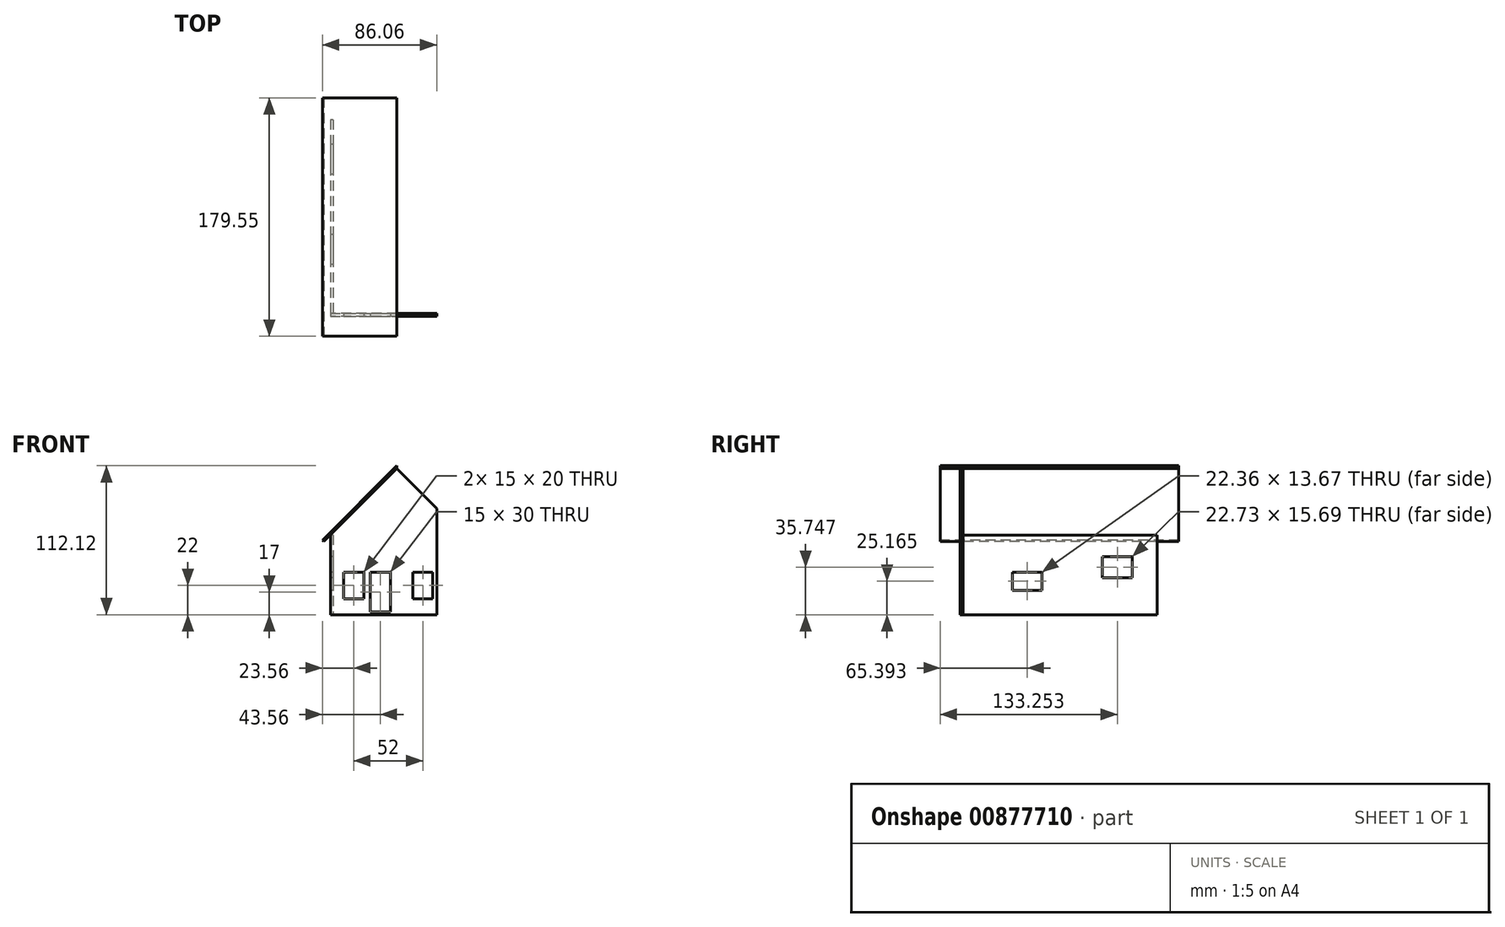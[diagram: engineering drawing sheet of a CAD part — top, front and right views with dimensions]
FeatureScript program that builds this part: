
annotation { "Feature Type Name" : "Feature", "Feature Type Description" : "" }
export const myFeature = defineFeature(function(context is Context, id is Id, definition is map)
    precondition{}
    {
        {
            var Q0;
            Q0=qCreatedBy(makeId("Top.planeOp"),FACE);
            var sketch = newSketch(context, id + "F0", { "sketchPlane" : qUnion([Q0])});
            skLineSegment(sketch, "E0.bottom", {"start": v(-80, 150) * mm, "end": v(0, 150) * mm});
            skLineSegment(sketch, "E0.top", {"start": v(-80, 0) * mm, "end": v(0, 0) * mm});
            skLineSegment(sketch, "E0.left", {"start": v(-80, 150) * mm, "end": v(-80, 0) * mm});
            skLineSegment(sketch, "E0.right", {"start": v(0, 150) * mm, "end": v(0, 0) * mm});
            skLineSegment(sketch, "E1", {"start": v(-80, 2) * mm, "end": v(0, 2) * mm});
            skLineSegment(sketch, "E2", {"start": v(-80, 148) * mm, "end": v(0, 148) * mm});
            skLineSegment(sketch, "E3", {"start": v(-78, 148) * mm, "end": v(-78, 2) * mm});
            skLineSegment(sketch, "E4", {"start": v(-2, 148) * mm, "end": v(-2, 2) * mm});
            skSolve(sketch);
        }
        {
            var Q0;
            Q0=qCreatedBy(makeId("Front.planeOp"),FACE);
            var sketch = newSketch(context, id + "F1", { "sketchPlane" : qUnion([Q0])});
            skLineSegment(sketch, "E5", {"start": v(-80, 0) * mm, "end": v(0, 0) * mm});
            skLineSegment(sketch, "E6", {"start": v(0, 0) * mm, "end": v(0, 80) * mm});
            skLineSegment(sketch, "E7", {"start": v(0, 80) * mm, "end": v(-30, 110) * mm});
            skLineSegment(sketch, "E8", {"start": v(-30, 110) * mm, "end": v(-80, 60) * mm});
            skLineSegment(sketch, "E9", {"start": v(-80, 60) * mm, "end": v(-80, 0) * mm});
            skLineSegment(sketch, "E10.bottom", {"start": v(-70, 32) * mm, "end": v(-55, 32) * mm});
            skLineSegment(sketch, "E10.top", {"start": v(-70, 12) * mm, "end": v(-55, 12) * mm});
            skLineSegment(sketch, "E10.left", {"start": v(-70, 32) * mm, "end": v(-70, 12) * mm});
            skLineSegment(sketch, "E10.right", {"start": v(-55, 32) * mm, "end": v(-55, 12) * mm});
            skLineSegment(sketch, "E11.bottom", {"start": v(-18, 32) * mm, "end": v(-3, 32) * mm});
            skLineSegment(sketch, "E11.top", {"start": v(-18, 12) * mm, "end": v(-3, 12) * mm});
            skLineSegment(sketch, "E11.left", {"start": v(-18, 32) * mm, "end": v(-18, 12) * mm});
            skLineSegment(sketch, "E11.right", {"start": v(-3, 32) * mm, "end": v(-3, 12) * mm});
            skLineSegment(sketch, "E12.bottom", {"start": v(-50, 32) * mm, "end": v(-35, 32) * mm});
            skLineSegment(sketch, "E12.top", {"start": v(-50, 2) * mm, "end": v(-35, 2) * mm});
            skLineSegment(sketch, "E12.left", {"start": v(-50, 32) * mm, "end": v(-50, 2) * mm});
            skLineSegment(sketch, "E12.right", {"start": v(-35, 32) * mm, "end": v(-35, 2) * mm});
            skSolve(sketch);
        }
        {
            var Q0;
            Q0=makeQuery(id+"F1.imprint","IMPRINT",FACE,{"disambiguationData":[TD([[makeQuery(id+"F1.imprint","IMPRINT",EDGE,{"derivedFrom":sQuery(id+"F1.wireOp",EDGE,"E5")}),1.0]])]});
            var Q1;
            Q1=sQuery(id+"F0.wireOp",VERTEX,"E1.end");
            extrude(context, id + "F2", {"entities" : qUnion([Q0]), "endBound" : BoundingType.UP_TO_VERTEX, "oppositeDirection" : true, "depth" : 25 * mm, "endBoundEntityVertex" : qUnion([Q1]), "offsetDistance" : 25 * mm});
        }
        {
            var Q0;
            Q0=qCreatedBy(makeId("Right.planeOp"),FACE);
            var Q1;
            Q1=sQuery(id+"F0.wireOp",VERTEX,"E0.top.start");
            cPlane(context, id + "F3", {"entities" : qUnion([Q0, Q1]), "cplaneType" : CPlaneType.PLANE_POINT, "offset" : 25 * mm, "width" : 150 * mm, "height" : 150 * mm});
        }
        {
            var Q0;
            Q0=qCreatedBy(id+"F3.planeOp",FACE);
            var sketch = newSketch(context, id + "F4", { "sketchPlane" : qUnion([Q0])});
            skLineSegment(sketch, "E13.bottom", {"start": v(148, 60) * mm, "end": v(2, 60) * mm});
            skLineSegment(sketch, "E13.top", {"start": v(148, 0) * mm, "end": v(2, 0) * mm});
            skLineSegment(sketch, "E13.left", {"start": v(148, 60) * mm, "end": v(148, 0) * mm});
            skLineSegment(sketch, "E13.right", {"start": v(2, 60) * mm, "end": v(2, 0) * mm});
            skLineSegment(sketch, "E14.bottom", {"start": v(129.5, 43.6) * mm, "end": v(106.78, 43.6) * mm});
            skLineSegment(sketch, "E14.top", {"start": v(129.5, 27.9) * mm, "end": v(106.78, 27.9) * mm});
            skLineSegment(sketch, "E14.left", {"start": v(129.5, 43.6) * mm, "end": v(129.5, 27.9) * mm});
            skLineSegment(sketch, "E14.right", {"start": v(106.78, 43.6) * mm, "end": v(106.78, 27.9) * mm});
            skLineSegment(sketch, "E15.bottom", {"start": v(61.46, 32) * mm, "end": v(39.1, 32) * mm});
            skLineSegment(sketch, "E15.top", {"start": v(61.46, 18.33) * mm, "end": v(39.1, 18.33) * mm});
            skLineSegment(sketch, "E15.left", {"start": v(61.46, 32) * mm, "end": v(61.46, 18.33) * mm});
            skLineSegment(sketch, "E15.right", {"start": v(39.1, 32) * mm, "end": v(39.1, 18.33) * mm});
            skLineSegment(sketch, "E16.bottom", {"start": v(164.44, 109.45) * mm, "end": v(-15.11, 109.45) * mm});
            skLineSegment(sketch, "E16.top", {"start": v(164.44, 62.44) * mm, "end": v(-15.11, 62.44) * mm});
            skLineSegment(sketch, "E16.left", {"start": v(164.44, 109.45) * mm, "end": v(164.44, 62.44) * mm});
            skLineSegment(sketch, "E16.right", {"start": v(-15.11, 109.45) * mm, "end": v(-15.11, 62.44) * mm});
            skSolve(sketch);
        }
        {
            var Q0;
            Q0=makeQuery(id+"F4.imprint","IMPRINT",FACE,{"disambiguationData":[TD([[makeQuery(id+"F4.imprint","IMPRINT",EDGE,{"derivedFrom":sQuery(id+"F4.wireOp",EDGE,"E13.bottom")}),1.0]])]});
            var Q1;
            Q1=sQuery(id+"F0.wireOp",VERTEX,"E3.end");
            extrude(context, id + "F5", {"entities" : qUnion([Q0]), "endBound" : BoundingType.UP_TO_VERTEX, "depth" : 25 * mm, "endBoundEntityVertex" : qUnion([Q1]), "offsetDistance" : 25 * mm});
        }
        {
            var Q0;
            Q0=qCreatedBy(makeId("Front.planeOp"),FACE);
            var sketch = newSketch(context, id + "F6", { "sketchPlane" : qUnion([Q0])});
            skLineSegment(sketch, "E17", {"start": v(-30, 112.12) * mm, "end": v(-30, 110) * mm});
            skLineSegment(sketch, "E18", {"start": v(-30, 110) * mm, "end": v(-85, 55) * mm});
            skLineSegment(sketch, "E19", {"start": v(-85, 55) * mm, "end": v(-86.06, 56.06) * mm});
            skLineSegment(sketch, "E20", {"start": v(-86.06, 56.06) * mm, "end": v(-30, 112.12) * mm});
            skSolve(sketch);
        }
        {
            var Q0;
            Q0=makeQuery(id+"F6.imprint","IMPRINT",FACE,{"disambiguationData":[TD([[makeQuery(id+"F6.imprint","IMPRINT",EDGE,{"derivedFrom":sQuery(id+"F6.wireOp",EDGE,"E17")}),-1.0]])]});
            var Q1;
            Q1=sQuery(id+"F4.wireOp",VERTEX,"E16.top.start");
            var Q2;
            Q2=sQuery(id+"F4.wireOp",VERTEX,"E16.bottom.end");
            extrude(context, id + "F7", {"entities" : qUnion([Q0]), "endBound" : BoundingType.UP_TO_VERTEX, "oppositeDirection" : true, "depth" : 25 * mm, "endBoundEntityVertex" : qUnion([Q1]), "offsetDistance" : 25 * mm, "hasSecondDirection" : true, "secondDirectionBound" : SecondDirectionBoundingType.UP_TO_VERTEX, "secondDirectionOppositeDirection" : false, "secondDirectionDepth" : 25 * mm, "secondDirectionBoundEntityVertex" : qUnion([Q2])});
        }
    });
